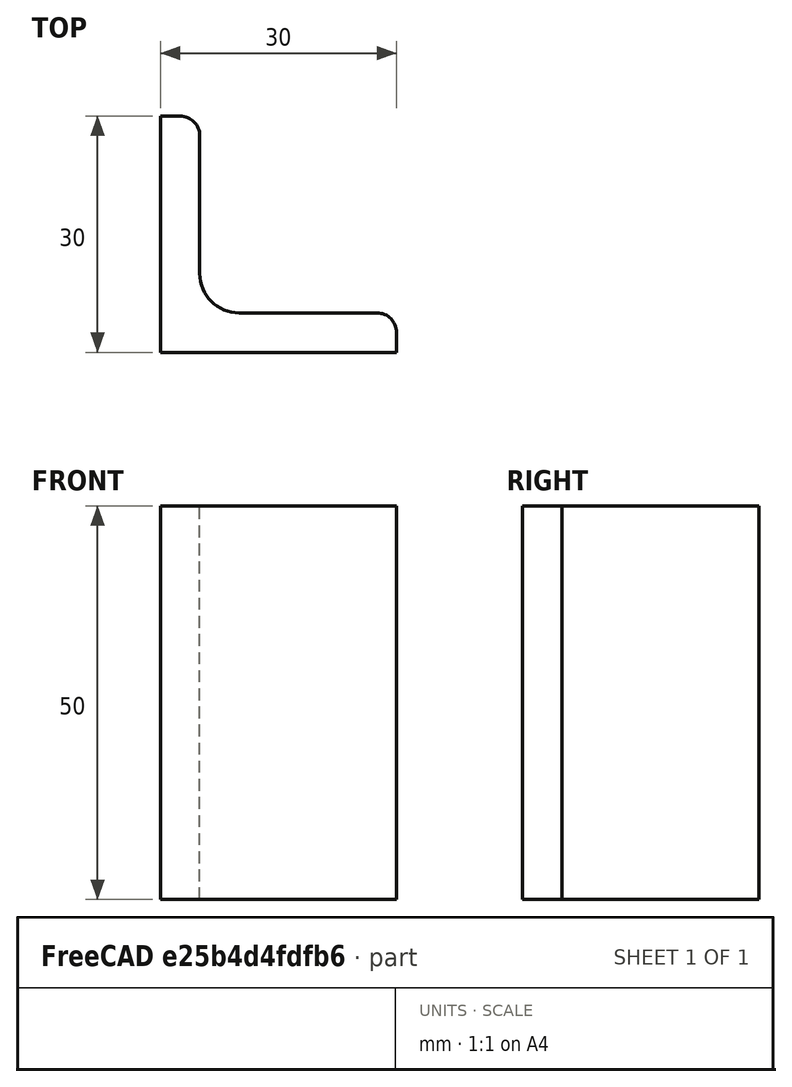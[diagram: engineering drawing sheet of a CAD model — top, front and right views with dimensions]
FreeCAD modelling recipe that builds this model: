
FCSTD DOCUMENT  (FreeCAD 0.15R4671 (Git))
Label: Angle Bar L30x30x5 EN10056 S235JR
License: All rights reserved
LicenseURL: http://en.wikipedia.org/wiki/All_rights_reserved
objects: Sketcher::SketchObject×1, Part::Extrusion×1
note: 2 computed .brp shape members not serialized (recipe doc carries the construction recipe); baked Part::Feature solids carry a one-line shape summary decoded from their .brp

FEATURE [Sketcher::SketchObject] Sketch
  sketch-geometry (9):
    g0: LineSegment StartX=0 StartY=0 StartZ=0 EndX=30 EndY=0 EndZ=0
    g1: LineSegment StartX=30 StartY=0 StartZ=0 EndX=30 EndY=2.5 EndZ=0
    g2: LineSegment StartX=27.5 StartY=5 StartZ=0 EndX=10 EndY=5 EndZ=0
    g3: LineSegment StartX=0 StartY=0 StartZ=0 EndX=0 EndY=30 EndZ=0
    g4: LineSegment StartX=0 StartY=30 StartZ=0 EndX=2.5 EndY=30 EndZ=0
    g5: LineSegment StartX=5 StartY=27.5 StartZ=0 EndX=5 EndY=10 EndZ=0
    g6: ArcOfCircle CenterX=10 CenterY=10 CenterZ=0 NormalX=0 NormalY=0 NormalZ=1 Radius=5 StartAngle=3.14159 EndAngle=4.71239
    g7: ArcOfCircle CenterX=2.5 CenterY=27.5 CenterZ=0 NormalX=0 NormalY=0 NormalZ=1 Radius=2.5 StartAngle=0 EndAngle=1.5708
    g8: ArcOfCircle CenterX=27.5 CenterY=2.5 CenterZ=0 NormalX=0 NormalY=0 NormalZ=1 Radius=2.5 StartAngle=0 EndAngle=1.5708
  constraints (23):
    c: Coincident(g0,g-1)
    c: Horizontal(g0)
    c: Coincident(g1,g0)
    c: Vertical(g1)
    c: Horizontal(g2)
    c: Coincident(g3,g-1)
    c: Vertical(g3)
    c: Coincident(g4,g3)
    c: Horizontal(g4)
    c: Vertical(g5)
    c: Tangent(g5,g6) = -1.5708
    c: Tangent(g2,g6) = 1.5708
    c: Tangent(g4,g7) = 1.5708
    c: Tangent(g5,g7) = 1.5708
    c: Tangent(g2,g8) = -1.5708
    c: Tangent(g1,g8) = -1.5708
    c: DistanceX(g0) = 30
    c: DistanceY(g3) = 30
    c: DistanceY(g0,g2) = 5
    c: DistanceX(g3,g5) = 5
    c: Radius(g6) = 5
    c: Radius(g8) = 2.5
    c: Radius(g7) = 2.5
FEATURE [Part::Extrusion] Extrude  label="Angle Bar L30x30x5 EN10056 S235JR"
  Base = -> Sketch
  Dir = (0,0,50)
  Solid = true
